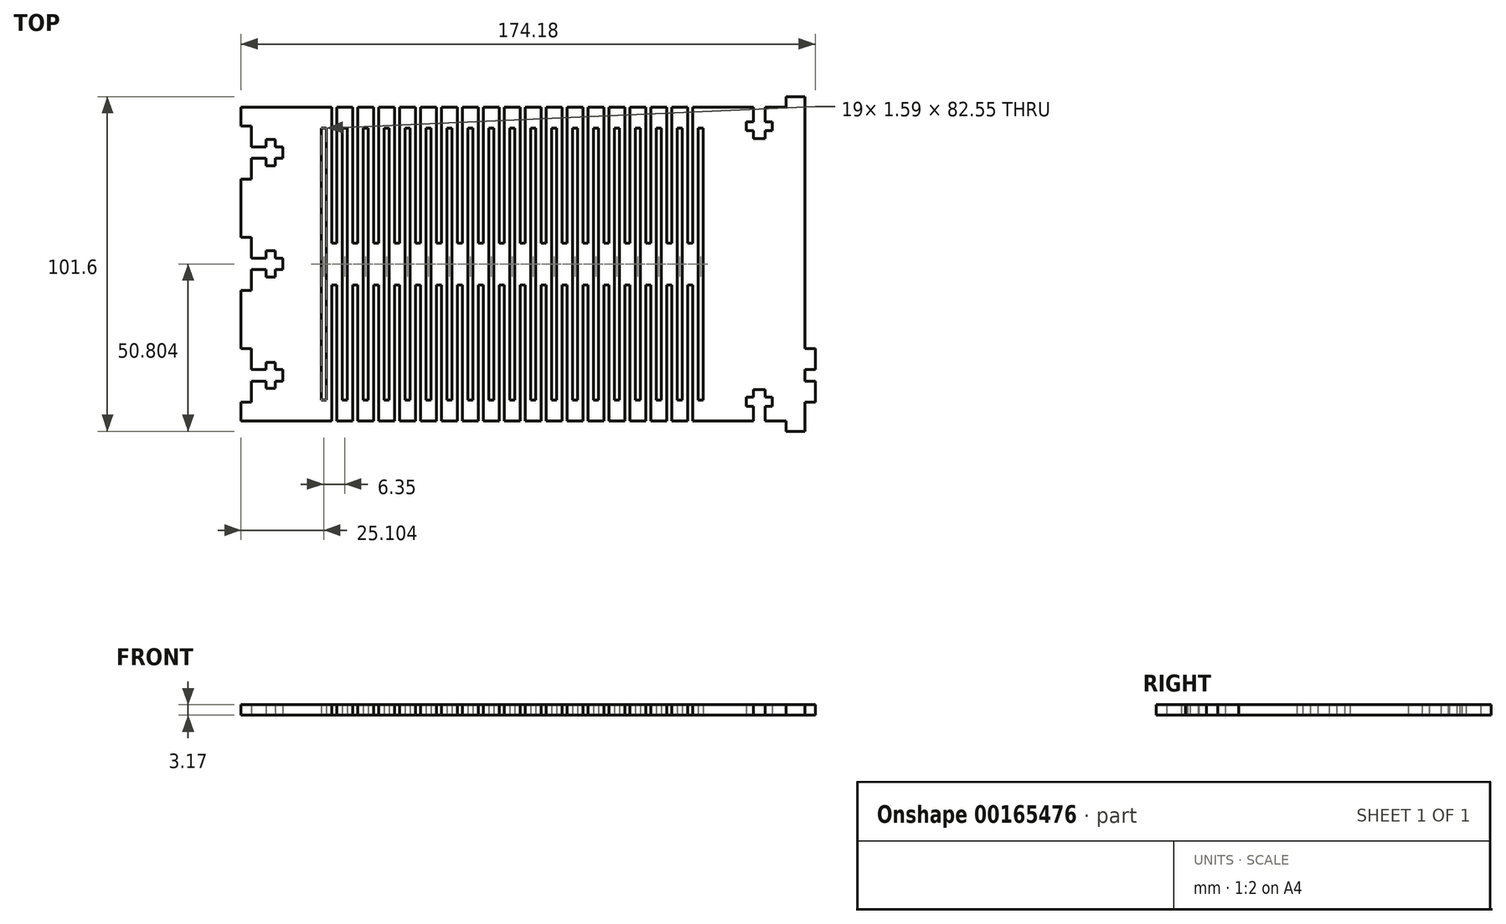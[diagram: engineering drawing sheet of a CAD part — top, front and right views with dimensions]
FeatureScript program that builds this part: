
annotation { "Feature Type Name" : "Feature", "Feature Type Description" : "" }
export const myFeature = defineFeature(function(context is Context, id is Id, definition is map)
    precondition{}
    {
        {
            var Q0;
            Q0=qCreatedBy(makeId("Top.planeOp"),FACE);
            var sketch = newSketch(context, id + "F0", { "sketchPlane" : qUnion([Q0])});
            skLineSegment(sketch, "E0.top", {"start": v(-188.02, -217.63) * mm, "end": v(-188.02, -116.03) * mm});
            skLineSegment(sketch, "E1.bottom", {"start": v(-188.02, -202.39) * mm, "end": v(-188.02, -198.88) * mm});
            skLineSegment(sketch, "E1.top", {"start": v(-175.32, -202.39) * mm, "end": v(-175.32, -198.88) * mm});
            skLineSegment(sketch, "E1.left", {"start": v(-188.02, -202.39) * mm, "end": v(-175.32, -202.39) * mm});
            skLineSegment(sketch, "E1.right", {"start": v(-188.02, -198.88) * mm, "end": v(-175.32, -198.88) * mm});
            skLineSegment(sketch, "E2.bottom", {"start": v(-177.62, -196.66) * mm, "end": v(-177.62, -204.6) * mm});
            skLineSegment(sketch, "E2.top", {"start": v(-180.4, -196.66) * mm, "end": v(-180.4, -204.6) * mm});
            skLineSegment(sketch, "E2.left", {"start": v(-177.62, -196.66) * mm, "end": v(-180.4, -196.66) * mm});
            skLineSegment(sketch, "E2.right", {"start": v(-177.62, -204.6) * mm, "end": v(-180.4, -204.6) * mm});
            skLineSegment(sketch, "E3.bottom", {"start": v(-188.02, -208.74) * mm, "end": v(-188.02, -192.53) * mm});
            skLineSegment(sketch, "E3.top", {"start": v(-184.84, -208.74) * mm, "end": v(-184.84, -192.53) * mm});
            skLineSegment(sketch, "E3.left", {"start": v(-188.02, -208.74) * mm, "end": v(-184.84, -208.74) * mm});
            skLineSegment(sketch, "E3.right", {"start": v(-188.02, -192.53) * mm, "end": v(-184.84, -192.53) * mm});
            skLineSegment(sketch, "E4.bottom", {"start": v(-188.02, -116.03) * mm, "end": v(-13.84, -116.03) * mm});
            skLineSegment(sketch, "E4.top", {"start": v(-188.02, -217.63) * mm, "end": v(-13.84, -217.63) * mm});
            skLineSegment(sketch, "E4.left", {"start": v(-188.02, -116.03) * mm, "end": v(-188.02, -217.63) * mm});
            skLineSegment(sketch, "E4.right", {"start": v(-13.84, -116.03) * mm, "end": v(-13.84, -217.63) * mm});
            skLineSegment(sketch, "E5.0.1.0", {"start": v(-188.02, -174.93) * mm, "end": v(-188.02, -158.72) * mm});
            skLineSegment(sketch, "E5.0.1.1", {"start": v(-184.84, -174.93) * mm, "end": v(-184.84, -158.72) * mm});
            skLineSegment(sketch, "E5.0.1.2", {"start": v(-188.02, -174.93) * mm, "end": v(-184.84, -174.93) * mm});
            skLineSegment(sketch, "E5.0.1.3", {"start": v(-175.32, -168.58) * mm, "end": v(-175.32, -165.07) * mm});
            skLineSegment(sketch, "E5.0.1.4", {"start": v(-188.02, -168.58) * mm, "end": v(-175.32, -168.58) * mm});
            skLineSegment(sketch, "E5.0.1.5", {"start": v(-188.02, -165.07) * mm, "end": v(-175.32, -165.07) * mm});
            skLineSegment(sketch, "E5.0.1.6", {"start": v(-177.62, -162.86) * mm, "end": v(-177.62, -170.8) * mm});
            skLineSegment(sketch, "E5.0.1.7", {"start": v(-180.4, -162.86) * mm, "end": v(-180.4, -170.8) * mm});
            skLineSegment(sketch, "E5.0.1.8", {"start": v(-177.62, -162.86) * mm, "end": v(-180.4, -162.86) * mm});
            skLineSegment(sketch, "E5.0.1.9", {"start": v(-177.62, -170.8) * mm, "end": v(-180.4, -170.8) * mm});
            skLineSegment(sketch, "E5.0.1.10", {"start": v(-188.02, -158.72) * mm, "end": v(-184.84, -158.72) * mm});
            skLineSegment(sketch, "E5.0.1.11", {"start": v(-188.02, -168.58) * mm, "end": v(-188.02, -165.07) * mm});
            skLineSegment(sketch, "E5.0.2.0", {"start": v(-188.02, -141.12) * mm, "end": v(-188.02, -124.92) * mm});
            skLineSegment(sketch, "E5.0.2.1", {"start": v(-184.84, -141.12) * mm, "end": v(-184.84, -124.92) * mm});
            skLineSegment(sketch, "E5.0.2.2", {"start": v(-188.02, -141.12) * mm, "end": v(-184.84, -141.12) * mm});
            skLineSegment(sketch, "E5.0.2.3", {"start": v(-175.32, -134.77) * mm, "end": v(-175.32, -131.27) * mm});
            skLineSegment(sketch, "E5.0.2.4", {"start": v(-188.02, -134.77) * mm, "end": v(-175.32, -134.77) * mm});
            skLineSegment(sketch, "E5.0.2.5", {"start": v(-188.02, -131.27) * mm, "end": v(-175.32, -131.27) * mm});
            skLineSegment(sketch, "E5.0.2.6", {"start": v(-177.62, -129.05) * mm, "end": v(-177.62, -136.99) * mm});
            skLineSegment(sketch, "E5.0.2.7", {"start": v(-180.4, -129.05) * mm, "end": v(-180.4, -136.99) * mm});
            skLineSegment(sketch, "E5.0.2.8", {"start": v(-177.62, -129.05) * mm, "end": v(-180.4, -129.05) * mm});
            skLineSegment(sketch, "E5.0.2.9", {"start": v(-177.62, -136.99) * mm, "end": v(-180.4, -136.99) * mm});
            skLineSegment(sketch, "E5.0.2.10", {"start": v(-188.02, -124.92) * mm, "end": v(-184.84, -124.92) * mm});
            skLineSegment(sketch, "E5.0.2.11", {"start": v(-188.02, -134.77) * mm, "end": v(-188.02, -131.27) * mm});
            skLineSegment(sketch, "E5.direction1", {"start": v(-188.02, -208.74) * mm, "end": v(-162.62, -208.74) * mm, "construction": true});
            skLineSegment(sketch, "E5.direction2", {"start": v(-188.02, -208.74) * mm, "end": v(-188.02, -174.93) * mm, "construction": true});
            skLineSegment(sketch, "E6.bottom", {"start": v(-13.84, -116.03) * mm, "end": v(-17.01, -116.03) * mm});
            skLineSegment(sketch, "E6.top", {"start": v(-13.84, -217.63) * mm, "end": v(-17.01, -217.63) * mm});
            skLineSegment(sketch, "E6.right", {"start": v(-17.01, -116.03) * mm, "end": v(-17.01, -217.63) * mm});
            skLineSegment(sketch, "E7.bottom", {"start": v(-17.01, -208.74) * mm, "end": v(-13.84, -208.74) * mm});
            skLineSegment(sketch, "E7.top", {"start": v(-17.01, -202.39) * mm, "end": v(-13.84, -202.39) * mm});
            skLineSegment(sketch, "E7.left", {"start": v(-17.01, -208.74) * mm, "end": v(-17.01, -202.39) * mm});
            skLineSegment(sketch, "E7.right", {"start": v(-13.84, -208.74) * mm, "end": v(-13.84, -202.39) * mm});
            skLineSegment(sketch, "E8.top", {"start": v(-17.01, -198.88) * mm, "end": v(-13.84, -198.88) * mm});
            skLineSegment(sketch, "E8.left", {"start": v(-17.01, -202.39) * mm, "end": v(-17.01, -198.88) * mm});
            skLineSegment(sketch, "E8.right", {"start": v(-13.84, -202.39) * mm, "end": v(-13.84, -198.88) * mm});
            skLineSegment(sketch, "E9.top", {"start": v(-17.01, -192.53) * mm, "end": v(-13.84, -192.53) * mm});
            skLineSegment(sketch, "E9.left", {"start": v(-17.01, -198.88) * mm, "end": v(-17.01, -192.53) * mm});
            skLineSegment(sketch, "E9.right", {"start": v(-13.84, -198.88) * mm, "end": v(-13.84, -192.53) * mm});
            skLineSegment(sketch, "E10.0.1.0", {"start": v(-13.84, -168.58) * mm, "end": v(-13.84, -165.07) * mm});
            skLineSegment(sketch, "E10.0.1.1", {"start": v(-17.01, -168.58) * mm, "end": v(-17.01, -165.07) * mm});
            skLineSegment(sketch, "E10.0.1.2", {"start": v(-17.01, -174.93) * mm, "end": v(-17.01, -168.58) * mm});
            skLineSegment(sketch, "E10.0.1.3", {"start": v(-17.01, -168.58) * mm, "end": v(-13.84, -168.58) * mm});
            skLineSegment(sketch, "E10.0.1.4", {"start": v(-17.01, -174.93) * mm, "end": v(-13.84, -174.93) * mm});
            skLineSegment(sketch, "E10.0.1.5", {"start": v(-13.84, -174.93) * mm, "end": v(-13.84, -168.58) * mm});
            skLineSegment(sketch, "E10.0.1.6", {"start": v(-13.84, -165.07) * mm, "end": v(-13.84, -158.72) * mm});
            skLineSegment(sketch, "E10.0.1.7", {"start": v(-17.01, -158.72) * mm, "end": v(-13.84, -158.72) * mm});
            skLineSegment(sketch, "E10.0.1.8", {"start": v(-17.01, -165.07) * mm, "end": v(-17.01, -158.72) * mm});
            skLineSegment(sketch, "E10.0.1.9", {"start": v(-17.01, -165.07) * mm, "end": v(-13.84, -165.07) * mm});
            skLineSegment(sketch, "E10.0.1.10", {"start": v(-17.01, -165.07) * mm, "end": v(-13.84, -165.07) * mm});
            skLineSegment(sketch, "E10.0.1.11", {"start": v(-17.01, -168.58) * mm, "end": v(-13.84, -168.58) * mm});
            skLineSegment(sketch, "E10.0.2.0", {"start": v(-13.84, -134.77) * mm, "end": v(-13.84, -131.27) * mm});
            skLineSegment(sketch, "E10.0.2.1", {"start": v(-17.01, -134.77) * mm, "end": v(-17.01, -131.27) * mm});
            skLineSegment(sketch, "E10.0.2.2", {"start": v(-17.01, -141.12) * mm, "end": v(-17.01, -134.77) * mm});
            skLineSegment(sketch, "E10.0.2.3", {"start": v(-17.01, -134.77) * mm, "end": v(-13.84, -134.77) * mm});
            skLineSegment(sketch, "E10.0.2.4", {"start": v(-17.01, -141.12) * mm, "end": v(-13.84, -141.12) * mm});
            skLineSegment(sketch, "E10.0.2.5", {"start": v(-13.84, -141.12) * mm, "end": v(-13.84, -134.77) * mm});
            skLineSegment(sketch, "E10.0.2.6", {"start": v(-13.84, -131.27) * mm, "end": v(-13.84, -124.92) * mm});
            skLineSegment(sketch, "E10.0.2.7", {"start": v(-17.01, -124.92) * mm, "end": v(-13.84, -124.92) * mm});
            skLineSegment(sketch, "E10.0.2.8", {"start": v(-17.01, -131.27) * mm, "end": v(-17.01, -124.92) * mm});
            skLineSegment(sketch, "E10.0.2.9", {"start": v(-17.01, -131.27) * mm, "end": v(-13.84, -131.27) * mm});
            skLineSegment(sketch, "E10.0.2.10", {"start": v(-17.01, -131.27) * mm, "end": v(-13.84, -131.27) * mm});
            skLineSegment(sketch, "E10.0.2.11", {"start": v(-17.01, -134.77) * mm, "end": v(-13.84, -134.77) * mm});
            skLineSegment(sketch, "E10.direction1", {"start": v(-17.01, -208.74) * mm, "end": v(373.75, -208.74) * mm, "construction": true});
            skLineSegment(sketch, "E10.direction2", {"start": v(-17.01, -208.74) * mm, "end": v(-17.01, -174.93) * mm, "construction": true});
            skLineSegment(sketch, "E11.top", {"start": v(-188.02, -119.2) * mm, "end": v(-13.84, -119.2) * mm});
            skLineSegment(sketch, "E11.left", {"start": v(-188.02, -116.03) * mm, "end": v(-188.02, -119.2) * mm});
            skLineSegment(sketch, "E11.right", {"start": v(-13.84, -116.03) * mm, "end": v(-13.84, -119.2) * mm});
            skLineSegment(sketch, "E12.top", {"start": v(-188.02, -214.45) * mm, "end": v(-13.84, -214.45) * mm});
            skLineSegment(sketch, "E12.left", {"start": v(-188.02, -217.63) * mm, "end": v(-188.02, -214.45) * mm});
            skLineSegment(sketch, "E12.right", {"start": v(-13.84, -217.63) * mm, "end": v(-13.84, -214.45) * mm});
            skLineSegment(sketch, "E13.bottom", {"start": v(-29.08, -217.63) * mm, "end": v(-32.58, -217.63) * mm});
            skLineSegment(sketch, "E13.top", {"start": v(-29.08, -204.93) * mm, "end": v(-32.58, -204.93) * mm});
            skLineSegment(sketch, "E13.left", {"start": v(-29.08, -217.63) * mm, "end": v(-29.08, -204.93) * mm});
            skLineSegment(sketch, "E13.right", {"start": v(-32.58, -217.63) * mm, "end": v(-32.58, -204.93) * mm});
            skLineSegment(sketch, "E14.bottom", {"start": v(-34.8, -207.23) * mm, "end": v(-26.86, -207.23) * mm});
            skLineSegment(sketch, "E14.top", {"start": v(-34.8, -210) * mm, "end": v(-26.86, -210) * mm});
            skLineSegment(sketch, "E14.left", {"start": v(-34.8, -207.23) * mm, "end": v(-34.8, -210) * mm});
            skLineSegment(sketch, "E14.right", {"start": v(-26.86, -207.23) * mm, "end": v(-26.86, -210) * mm});
            skLineSegment(sketch, "E15.bottom", {"start": v(-22.73, -217.63) * mm, "end": v(-38.93, -217.63) * mm});
            skLineSegment(sketch, "E15.top", {"start": v(-22.73, -214.45) * mm, "end": v(-38.93, -214.45) * mm});
            skLineSegment(sketch, "E15.left", {"start": v(-22.73, -217.63) * mm, "end": v(-22.73, -214.45) * mm});
            skLineSegment(sketch, "E15.right", {"start": v(-38.93, -217.63) * mm, "end": v(-38.93, -214.45) * mm});
            skLineSegment(sketch, "E16", {"start": v(366.52, -166.83) * mm, "end": v(393.67, -166.83) * mm});
            skLineSegment(sketch, "E17.MirrorCS", {"start": v(-29.08, -116.03) * mm, "end": v(-32.58, -116.03) * mm});
            skLineSegment(sketch, "E18.MirrorCS", {"start": v(-29.08, -128.73) * mm, "end": v(-32.58, -128.73) * mm});
            skLineSegment(sketch, "E19.MirrorCS", {"start": v(-29.08, -116.03) * mm, "end": v(-29.08, -128.73) * mm});
            skLineSegment(sketch, "E20.MirrorCS", {"start": v(-32.58, -116.03) * mm, "end": v(-32.58, -128.73) * mm});
            skLineSegment(sketch, "E21.MirrorCS", {"start": v(-34.8, -126.42) * mm, "end": v(-26.86, -126.42) * mm});
            skLineSegment(sketch, "E22.MirrorCS", {"start": v(-34.8, -123.65) * mm, "end": v(-26.86, -123.65) * mm});
            skLineSegment(sketch, "E23.MirrorCS", {"start": v(-22.73, -116.03) * mm, "end": v(-38.93, -116.03) * mm});
            skLineSegment(sketch, "E24.MirrorCS", {"start": v(-26.86, -126.42) * mm, "end": v(-26.86, -123.65) * mm});
            skLineSegment(sketch, "E25.MirrorCS", {"start": v(-34.8, -126.42) * mm, "end": v(-34.8, -123.65) * mm});
            skLineSegment(sketch, "E26.MirrorCS", {"start": v(-22.73, -119.2) * mm, "end": v(-38.93, -119.2) * mm});
            skLineSegment(sketch, "E27.MirrorCS", {"start": v(-22.73, -116.03) * mm, "end": v(-22.73, -119.2) * mm});
            skLineSegment(sketch, "E28.MirrorCS", {"start": v(-38.93, -116.03) * mm, "end": v(-38.93, -119.2) * mm});
            skLineSegment(sketch, "E29.bottom", {"start": v(-38.93, -119.2) * mm, "end": v(-47.82, -119.2) * mm});
            skLineSegment(sketch, "E29.top", {"start": v(-38.93, -116.03) * mm, "end": v(-47.82, -116.03) * mm});
            skLineSegment(sketch, "E29.left", {"start": v(-38.93, -119.2) * mm, "end": v(-38.93, -116.03) * mm});
            skLineSegment(sketch, "E29.right", {"start": v(-47.82, -119.2) * mm, "end": v(-47.82, -116.03) * mm});
            skLineSegment(sketch, "E30.bottom", {"start": v(-38.93, -217.63) * mm, "end": v(-47.82, -217.63) * mm});
            skLineSegment(sketch, "E30.top", {"start": v(-38.93, -214.45) * mm, "end": v(-47.82, -214.45) * mm});
            skLineSegment(sketch, "E30.right", {"start": v(-47.82, -217.63) * mm, "end": v(-47.82, -214.45) * mm});
            skLineSegment(sketch, "E31.bottom", {"start": v(-179.13, -217.63) * mm, "end": v(-172.78, -217.63) * mm});
            skLineSegment(sketch, "E31.top", {"start": v(-179.13, -214.45) * mm, "end": v(-172.78, -214.45) * mm});
            skLineSegment(sketch, "E31.left", {"start": v(-179.13, -217.63) * mm, "end": v(-179.13, -214.45) * mm});
            skLineSegment(sketch, "E31.right", {"start": v(-172.78, -217.63) * mm, "end": v(-172.78, -214.45) * mm});
            skLineSegment(sketch, "E32.bottom", {"start": v(-172.78, -217.63) * mm, "end": v(-169.27, -217.63) * mm});
            skLineSegment(sketch, "E32.top", {"start": v(-172.78, -214.45) * mm, "end": v(-169.27, -214.45) * mm});
            skLineSegment(sketch, "E32.right", {"start": v(-169.27, -217.63) * mm, "end": v(-169.27, -214.45) * mm});
            skLineSegment(sketch, "E33.bottom", {"start": v(-169.27, -217.63) * mm, "end": v(-162.92, -217.63) * mm});
            skLineSegment(sketch, "E33.top", {"start": v(-169.27, -214.45) * mm, "end": v(-162.92, -214.45) * mm});
            skLineSegment(sketch, "E33.right", {"start": v(-162.92, -217.63) * mm, "end": v(-162.92, -214.45) * mm});
            skLineSegment(sketch, "E34.MirrorCS", {"start": v(-172.78, -116.03) * mm, "end": v(-172.78, -119.2) * mm});
            skLineSegment(sketch, "E35.MirrorCS", {"start": v(-169.27, -116.03) * mm, "end": v(-169.27, -119.2) * mm});
            skLineSegment(sketch, "E36.MirrorCS", {"start": v(-179.13, -116.03) * mm, "end": v(-172.78, -116.03) * mm});
            skLineSegment(sketch, "E37.MirrorCS", {"start": v(-179.13, -119.2) * mm, "end": v(-172.78, -119.2) * mm});
            skLineSegment(sketch, "E38.MirrorCS", {"start": v(-179.13, -116.03) * mm, "end": v(-179.13, -119.2) * mm});
            skLineSegment(sketch, "E39.MirrorCS", {"start": v(-169.27, -116.03) * mm, "end": v(-162.92, -116.03) * mm});
            skLineSegment(sketch, "E40.MirrorCS", {"start": v(-172.78, -116.03) * mm, "end": v(-169.27, -116.03) * mm});
            skLineSegment(sketch, "E41.MirrorCS", {"start": v(-169.27, -119.2) * mm, "end": v(-162.92, -119.2) * mm});
            skLineSegment(sketch, "E42.MirrorCS", {"start": v(-162.92, -116.03) * mm, "end": v(-162.92, -119.2) * mm});
            skLineSegment(sketch, "E43.MirrorCS", {"start": v(-172.78, -119.2) * mm, "end": v(-169.27, -119.2) * mm});
            skLineSegment(sketch, "E44.bottom", {"start": v(-52.58, -116.03) * mm, "end": v(-51, -116.03) * mm});
            skLineSegment(sketch, "E44.top", {"start": v(-52.58, -160.48) * mm, "end": v(-51, -160.48) * mm});
            skLineSegment(sketch, "E44.left", {"start": v(-52.58, -116.03) * mm, "end": v(-52.58, -160.48) * mm});
            skLineSegment(sketch, "E44.right", {"start": v(-51, -116.03) * mm, "end": v(-51, -160.48) * mm});
            skLineSegment(sketch, "E45.bottom", {"start": v(-52.58, -217.63) * mm, "end": v(-51, -217.63) * mm});
            skLineSegment(sketch, "E45.top", {"start": v(-52.58, -173.18) * mm, "end": v(-51, -173.18) * mm});
            skLineSegment(sketch, "E45.left", {"start": v(-52.58, -217.63) * mm, "end": v(-52.58, -173.18) * mm});
            skLineSegment(sketch, "E45.right", {"start": v(-51, -217.63) * mm, "end": v(-51, -173.18) * mm});
            skLineSegment(sketch, "E46.bottom", {"start": v(-49.4, -125.55) * mm, "end": v(-47.82, -125.55) * mm});
            skLineSegment(sketch, "E46.top", {"start": v(-49.4, -208.1) * mm, "end": v(-47.82, -208.1) * mm});
            skLineSegment(sketch, "E46.left", {"start": v(-49.4, -125.55) * mm, "end": v(-49.4, -208.1) * mm});
            skLineSegment(sketch, "E46.right", {"start": v(-47.82, -125.55) * mm, "end": v(-47.82, -208.1) * mm});
            skLineSegment(sketch, "E47.1.0.0", {"start": v(-57.35, -217.63) * mm, "end": v(-57.35, -173.18) * mm});
            skLineSegment(sketch, "E47.1.0.1", {"start": v(-57.35, -116.03) * mm, "end": v(-57.35, -160.48) * mm});
            skLineSegment(sketch, "E47.1.0.2", {"start": v(-54.17, -125.55) * mm, "end": v(-54.17, -208.1) * mm});
            skLineSegment(sketch, "E47.1.0.3", {"start": v(-58.93, -116.03) * mm, "end": v(-58.93, -160.48) * mm});
            skLineSegment(sketch, "E47.1.0.4", {"start": v(-55.76, -125.55) * mm, "end": v(-55.76, -208.1) * mm});
            skLineSegment(sketch, "E47.1.0.5", {"start": v(-58.93, -217.63) * mm, "end": v(-58.93, -173.18) * mm});
            skLineSegment(sketch, "E47.1.0.6", {"start": v(-58.93, -116.03) * mm, "end": v(-57.35, -116.03) * mm});
            skLineSegment(sketch, "E47.1.0.7", {"start": v(-58.93, -217.63) * mm, "end": v(-57.35, -217.63) * mm});
            skLineSegment(sketch, "E47.1.0.8", {"start": v(-58.93, -173.18) * mm, "end": v(-57.35, -173.18) * mm});
            skLineSegment(sketch, "E47.1.0.9", {"start": v(-58.93, -160.48) * mm, "end": v(-57.35, -160.48) * mm});
            skLineSegment(sketch, "E47.1.0.10", {"start": v(-55.76, -208.1) * mm, "end": v(-54.17, -208.1) * mm});
            skLineSegment(sketch, "E47.1.0.11", {"start": v(-55.76, -125.55) * mm, "end": v(-54.17, -125.55) * mm});
            skLineSegment(sketch, "E47.2.0.0", {"start": v(-63.7, -217.63) * mm, "end": v(-63.7, -173.18) * mm});
            skLineSegment(sketch, "E47.2.0.1", {"start": v(-63.7, -116.03) * mm, "end": v(-63.7, -160.48) * mm});
            skLineSegment(sketch, "E47.2.0.2", {"start": v(-60.52, -125.55) * mm, "end": v(-60.52, -208.1) * mm});
            skLineSegment(sketch, "E47.2.0.3", {"start": v(-65.28, -116.03) * mm, "end": v(-65.28, -160.48) * mm});
            skLineSegment(sketch, "E47.2.0.4", {"start": v(-62.1, -125.55) * mm, "end": v(-62.1, -208.1) * mm});
            skLineSegment(sketch, "E47.2.0.5", {"start": v(-65.28, -217.63) * mm, "end": v(-65.28, -173.18) * mm});
            skLineSegment(sketch, "E47.2.0.6", {"start": v(-65.28, -116.03) * mm, "end": v(-63.7, -116.03) * mm});
            skLineSegment(sketch, "E47.2.0.7", {"start": v(-65.28, -217.63) * mm, "end": v(-63.7, -217.63) * mm});
            skLineSegment(sketch, "E47.2.0.8", {"start": v(-65.28, -173.18) * mm, "end": v(-63.7, -173.18) * mm});
            skLineSegment(sketch, "E47.2.0.9", {"start": v(-65.28, -160.48) * mm, "end": v(-63.7, -160.48) * mm});
            skLineSegment(sketch, "E47.2.0.10", {"start": v(-62.1, -208.1) * mm, "end": v(-60.52, -208.1) * mm});
            skLineSegment(sketch, "E47.2.0.11", {"start": v(-62.1, -125.55) * mm, "end": v(-60.52, -125.55) * mm});
            skLineSegment(sketch, "E47.3.0.0", {"start": v(-70.05, -217.63) * mm, "end": v(-70.05, -173.18) * mm});
            skLineSegment(sketch, "E47.3.0.1", {"start": v(-70.05, -116.03) * mm, "end": v(-70.05, -160.48) * mm});
            skLineSegment(sketch, "E47.3.0.2", {"start": v(-66.87, -125.55) * mm, "end": v(-66.87, -208.1) * mm});
            skLineSegment(sketch, "E47.3.0.3", {"start": v(-71.63, -116.03) * mm, "end": v(-71.63, -160.48) * mm});
            skLineSegment(sketch, "E47.3.0.4", {"start": v(-68.46, -125.55) * mm, "end": v(-68.46, -208.1) * mm});
            skLineSegment(sketch, "E47.3.0.5", {"start": v(-71.63, -217.63) * mm, "end": v(-71.63, -173.18) * mm});
            skLineSegment(sketch, "E47.3.0.6", {"start": v(-71.63, -116.03) * mm, "end": v(-70.05, -116.03) * mm});
            skLineSegment(sketch, "E47.3.0.7", {"start": v(-71.63, -217.63) * mm, "end": v(-70.05, -217.63) * mm});
            skLineSegment(sketch, "E47.3.0.8", {"start": v(-71.63, -173.18) * mm, "end": v(-70.05, -173.18) * mm});
            skLineSegment(sketch, "E47.3.0.9", {"start": v(-71.63, -160.48) * mm, "end": v(-70.05, -160.48) * mm});
            skLineSegment(sketch, "E47.3.0.10", {"start": v(-68.46, -208.1) * mm, "end": v(-66.87, -208.1) * mm});
            skLineSegment(sketch, "E47.3.0.11", {"start": v(-68.46, -125.55) * mm, "end": v(-66.87, -125.55) * mm});
            skLineSegment(sketch, "E47.4.0.0", {"start": v(-76.4, -217.63) * mm, "end": v(-76.4, -173.18) * mm});
            skLineSegment(sketch, "E47.4.0.1", {"start": v(-76.4, -116.03) * mm, "end": v(-76.4, -160.48) * mm});
            skLineSegment(sketch, "E47.4.0.2", {"start": v(-73.22, -125.55) * mm, "end": v(-73.22, -208.1) * mm});
            skLineSegment(sketch, "E47.4.0.3", {"start": v(-77.98, -116.03) * mm, "end": v(-77.98, -160.48) * mm});
            skLineSegment(sketch, "E47.4.0.4", {"start": v(-74.8, -125.55) * mm, "end": v(-74.8, -208.1) * mm});
            skLineSegment(sketch, "E47.4.0.5", {"start": v(-77.98, -217.63) * mm, "end": v(-77.98, -173.18) * mm});
            skLineSegment(sketch, "E47.4.0.6", {"start": v(-77.98, -116.03) * mm, "end": v(-76.4, -116.03) * mm});
            skLineSegment(sketch, "E47.4.0.7", {"start": v(-77.98, -217.63) * mm, "end": v(-76.4, -217.63) * mm});
            skLineSegment(sketch, "E47.4.0.8", {"start": v(-77.98, -173.18) * mm, "end": v(-76.4, -173.18) * mm});
            skLineSegment(sketch, "E47.4.0.9", {"start": v(-77.98, -160.48) * mm, "end": v(-76.4, -160.48) * mm});
            skLineSegment(sketch, "E47.4.0.10", {"start": v(-74.8, -208.1) * mm, "end": v(-73.22, -208.1) * mm});
            skLineSegment(sketch, "E47.4.0.11", {"start": v(-74.8, -125.55) * mm, "end": v(-73.22, -125.55) * mm});
            skLineSegment(sketch, "E47.5.0.0", {"start": v(-82.75, -217.63) * mm, "end": v(-82.75, -173.18) * mm});
            skLineSegment(sketch, "E47.5.0.1", {"start": v(-82.75, -116.03) * mm, "end": v(-82.75, -160.48) * mm});
            skLineSegment(sketch, "E47.5.0.2", {"start": v(-79.57, -125.55) * mm, "end": v(-79.57, -208.1) * mm});
            skLineSegment(sketch, "E47.5.0.3", {"start": v(-84.33, -116.03) * mm, "end": v(-84.33, -160.48) * mm});
            skLineSegment(sketch, "E47.5.0.4", {"start": v(-81.16, -125.55) * mm, "end": v(-81.16, -208.1) * mm});
            skLineSegment(sketch, "E47.5.0.5", {"start": v(-84.33, -217.63) * mm, "end": v(-84.33, -173.18) * mm});
            skLineSegment(sketch, "E47.5.0.6", {"start": v(-84.33, -116.03) * mm, "end": v(-82.75, -116.03) * mm});
            skLineSegment(sketch, "E47.5.0.7", {"start": v(-84.33, -217.63) * mm, "end": v(-82.75, -217.63) * mm});
            skLineSegment(sketch, "E47.5.0.8", {"start": v(-84.33, -173.18) * mm, "end": v(-82.75, -173.18) * mm});
            skLineSegment(sketch, "E47.5.0.9", {"start": v(-84.33, -160.48) * mm, "end": v(-82.75, -160.48) * mm});
            skLineSegment(sketch, "E47.5.0.10", {"start": v(-81.16, -208.1) * mm, "end": v(-79.57, -208.1) * mm});
            skLineSegment(sketch, "E47.5.0.11", {"start": v(-81.16, -125.55) * mm, "end": v(-79.57, -125.55) * mm});
            skLineSegment(sketch, "E47.6.0.0", {"start": v(-89.1, -217.63) * mm, "end": v(-89.1, -173.18) * mm});
            skLineSegment(sketch, "E47.6.0.1", {"start": v(-89.1, -116.03) * mm, "end": v(-89.1, -160.48) * mm});
            skLineSegment(sketch, "E47.6.0.2", {"start": v(-85.92, -125.55) * mm, "end": v(-85.92, -208.1) * mm});
            skLineSegment(sketch, "E47.6.0.3", {"start": v(-90.68, -116.03) * mm, "end": v(-90.68, -160.48) * mm});
            skLineSegment(sketch, "E47.6.0.4", {"start": v(-87.5, -125.55) * mm, "end": v(-87.5, -208.1) * mm});
            skLineSegment(sketch, "E47.6.0.5", {"start": v(-90.68, -217.63) * mm, "end": v(-90.68, -173.18) * mm});
            skLineSegment(sketch, "E47.6.0.6", {"start": v(-90.68, -116.03) * mm, "end": v(-89.1, -116.03) * mm});
            skLineSegment(sketch, "E47.6.0.7", {"start": v(-90.68, -217.63) * mm, "end": v(-89.1, -217.63) * mm});
            skLineSegment(sketch, "E47.6.0.8", {"start": v(-90.68, -173.18) * mm, "end": v(-89.1, -173.18) * mm});
            skLineSegment(sketch, "E47.6.0.9", {"start": v(-90.68, -160.48) * mm, "end": v(-89.1, -160.48) * mm});
            skLineSegment(sketch, "E47.6.0.10", {"start": v(-87.5, -208.1) * mm, "end": v(-85.92, -208.1) * mm});
            skLineSegment(sketch, "E47.6.0.11", {"start": v(-87.5, -125.55) * mm, "end": v(-85.92, -125.55) * mm});
            skLineSegment(sketch, "E47.7.0.0", {"start": v(-95.45, -217.63) * mm, "end": v(-95.45, -173.18) * mm});
            skLineSegment(sketch, "E47.7.0.1", {"start": v(-95.45, -116.03) * mm, "end": v(-95.45, -160.48) * mm});
            skLineSegment(sketch, "E47.7.0.2", {"start": v(-92.27, -125.55) * mm, "end": v(-92.27, -208.1) * mm});
            skLineSegment(sketch, "E47.7.0.3", {"start": v(-97.03, -116.03) * mm, "end": v(-97.03, -160.48) * mm});
            skLineSegment(sketch, "E47.7.0.4", {"start": v(-93.86, -125.55) * mm, "end": v(-93.86, -208.1) * mm});
            skLineSegment(sketch, "E47.7.0.5", {"start": v(-97.03, -217.63) * mm, "end": v(-97.03, -173.18) * mm});
            skLineSegment(sketch, "E47.7.0.6", {"start": v(-97.03, -116.03) * mm, "end": v(-95.45, -116.03) * mm});
            skLineSegment(sketch, "E47.7.0.7", {"start": v(-97.03, -217.63) * mm, "end": v(-95.45, -217.63) * mm});
            skLineSegment(sketch, "E47.7.0.8", {"start": v(-97.03, -173.18) * mm, "end": v(-95.45, -173.18) * mm});
            skLineSegment(sketch, "E47.7.0.9", {"start": v(-97.03, -160.48) * mm, "end": v(-95.45, -160.48) * mm});
            skLineSegment(sketch, "E47.7.0.10", {"start": v(-93.86, -208.1) * mm, "end": v(-92.27, -208.1) * mm});
            skLineSegment(sketch, "E47.7.0.11", {"start": v(-93.86, -125.55) * mm, "end": v(-92.27, -125.55) * mm});
            skLineSegment(sketch, "E47.direction1", {"start": v(-52.58, -217.63) * mm, "end": v(-58.93, -217.63) * mm, "construction": true});
            skLineSegment(sketch, "E48.bottom", {"start": v(-162.92, -119.2) * mm, "end": v(-155.3, -119.2) * mm});
            skLineSegment(sketch, "E48.top", {"start": v(-162.92, -116.03) * mm, "end": v(-155.3, -116.03) * mm});
            skLineSegment(sketch, "E48.left", {"start": v(-162.92, -119.2) * mm, "end": v(-162.92, -116.03) * mm});
            skLineSegment(sketch, "E49.6.8.0", {"start": v(-98.62, -125.55) * mm, "end": v(-98.62, -208.1) * mm});
            skLineSegment(sketch, "E49.12.8.0", {"start": v(-100.2, -125.55) * mm, "end": v(-100.2, -208.1) * mm});
            skLineSegment(sketch, "E49.30.8.0", {"start": v(-100.2, -208.1) * mm, "end": v(-98.62, -208.1) * mm});
            skLineSegment(sketch, "E49.33.8.0", {"start": v(-100.2, -125.55) * mm, "end": v(-98.62, -125.55) * mm});
            skLineSegment(sketch, "E50.0.9.0", {"start": v(-108.15, -217.63) * mm, "end": v(-108.15, -173.18) * mm});
            skLineSegment(sketch, "E50.3.9.0", {"start": v(-108.15, -116.03) * mm, "end": v(-108.15, -160.48) * mm});
            skLineSegment(sketch, "E50.6.9.0", {"start": v(-104.97, -125.55) * mm, "end": v(-104.97, -208.1) * mm});
            skLineSegment(sketch, "E50.9.9.0", {"start": v(-109.73, -116.03) * mm, "end": v(-109.73, -160.48) * mm});
            skLineSegment(sketch, "E50.12.9.0", {"start": v(-106.56, -125.55) * mm, "end": v(-106.56, -208.1) * mm});
            skLineSegment(sketch, "E50.15.9.0", {"start": v(-109.73, -217.63) * mm, "end": v(-109.73, -173.18) * mm});
            skLineSegment(sketch, "E50.18.9.0", {"start": v(-109.73, -116.03) * mm, "end": v(-108.15, -116.03) * mm});
            skLineSegment(sketch, "E50.21.9.0", {"start": v(-109.73, -217.63) * mm, "end": v(-108.15, -217.63) * mm});
            skLineSegment(sketch, "E50.24.9.0", {"start": v(-109.73, -173.18) * mm, "end": v(-108.15, -173.18) * mm});
            skLineSegment(sketch, "E50.27.9.0", {"start": v(-109.73, -160.48) * mm, "end": v(-108.15, -160.48) * mm});
            skLineSegment(sketch, "E50.30.9.0", {"start": v(-106.56, -208.1) * mm, "end": v(-104.97, -208.1) * mm});
            skLineSegment(sketch, "E50.33.9.0", {"start": v(-106.56, -125.55) * mm, "end": v(-104.97, -125.55) * mm});
            skLineSegment(sketch, "E51.0.10.0", {"start": v(-114.5, -217.63) * mm, "end": v(-114.5, -173.18) * mm});
            skLineSegment(sketch, "E51.3.10.0", {"start": v(-114.5, -116.03) * mm, "end": v(-114.5, -160.48) * mm});
            skLineSegment(sketch, "E51.6.10.0", {"start": v(-111.32, -125.55) * mm, "end": v(-111.32, -208.1) * mm});
            skLineSegment(sketch, "E51.9.10.0", {"start": v(-116.08, -116.03) * mm, "end": v(-116.08, -160.48) * mm});
            skLineSegment(sketch, "E51.12.10.0", {"start": v(-112.9, -125.55) * mm, "end": v(-112.9, -208.1) * mm});
            skLineSegment(sketch, "E51.15.10.0", {"start": v(-116.08, -217.63) * mm, "end": v(-116.08, -173.18) * mm});
            skLineSegment(sketch, "E51.18.10.0", {"start": v(-116.08, -116.03) * mm, "end": v(-114.5, -116.03) * mm});
            skLineSegment(sketch, "E51.21.10.0", {"start": v(-116.08, -217.63) * mm, "end": v(-114.5, -217.63) * mm});
            skLineSegment(sketch, "E51.24.10.0", {"start": v(-116.08, -173.18) * mm, "end": v(-114.5, -173.18) * mm});
            skLineSegment(sketch, "E51.27.10.0", {"start": v(-116.08, -160.48) * mm, "end": v(-114.5, -160.48) * mm});
            skLineSegment(sketch, "E51.30.10.0", {"start": v(-112.9, -208.1) * mm, "end": v(-111.32, -208.1) * mm});
            skLineSegment(sketch, "E51.33.10.0", {"start": v(-112.9, -125.55) * mm, "end": v(-111.32, -125.55) * mm});
            skLineSegment(sketch, "E51.0.11.0", {"start": v(-120.85, -217.63) * mm, "end": v(-120.85, -173.18) * mm});
            skLineSegment(sketch, "E51.3.11.0", {"start": v(-120.85, -116.03) * mm, "end": v(-120.85, -160.48) * mm});
            skLineSegment(sketch, "E51.6.11.0", {"start": v(-117.67, -125.55) * mm, "end": v(-117.67, -208.1) * mm});
            skLineSegment(sketch, "E51.9.11.0", {"start": v(-122.43, -116.03) * mm, "end": v(-122.43, -160.48) * mm});
            skLineSegment(sketch, "E51.12.11.0", {"start": v(-119.26, -125.55) * mm, "end": v(-119.26, -208.1) * mm});
            skLineSegment(sketch, "E51.15.11.0", {"start": v(-122.43, -217.63) * mm, "end": v(-122.43, -173.18) * mm});
            skLineSegment(sketch, "E51.18.11.0", {"start": v(-122.43, -116.03) * mm, "end": v(-120.85, -116.03) * mm});
            skLineSegment(sketch, "E51.21.11.0", {"start": v(-122.43, -217.63) * mm, "end": v(-120.85, -217.63) * mm});
            skLineSegment(sketch, "E51.24.11.0", {"start": v(-122.43, -173.18) * mm, "end": v(-120.85, -173.18) * mm});
            skLineSegment(sketch, "E51.27.11.0", {"start": v(-122.43, -160.48) * mm, "end": v(-120.85, -160.48) * mm});
            skLineSegment(sketch, "E51.30.11.0", {"start": v(-119.26, -208.1) * mm, "end": v(-117.67, -208.1) * mm});
            skLineSegment(sketch, "E51.33.11.0", {"start": v(-119.26, -125.55) * mm, "end": v(-117.67, -125.55) * mm});
            skLineSegment(sketch, "E51.0.12.0", {"start": v(-127.2, -217.63) * mm, "end": v(-127.2, -173.18) * mm});
            skLineSegment(sketch, "E51.3.12.0", {"start": v(-127.2, -116.03) * mm, "end": v(-127.2, -160.48) * mm});
            skLineSegment(sketch, "E51.6.12.0", {"start": v(-124.02, -125.55) * mm, "end": v(-124.02, -208.1) * mm});
            skLineSegment(sketch, "E51.9.12.0", {"start": v(-128.78, -116.03) * mm, "end": v(-128.78, -160.48) * mm});
            skLineSegment(sketch, "E51.12.12.0", {"start": v(-125.6, -125.55) * mm, "end": v(-125.6, -208.1) * mm});
            skLineSegment(sketch, "E51.15.12.0", {"start": v(-128.78, -217.63) * mm, "end": v(-128.78, -173.18) * mm});
            skLineSegment(sketch, "E51.18.12.0", {"start": v(-128.78, -116.03) * mm, "end": v(-127.2, -116.03) * mm});
            skLineSegment(sketch, "E51.21.12.0", {"start": v(-128.78, -217.63) * mm, "end": v(-127.2, -217.63) * mm});
            skLineSegment(sketch, "E51.24.12.0", {"start": v(-128.78, -173.18) * mm, "end": v(-127.2, -173.18) * mm});
            skLineSegment(sketch, "E51.27.12.0", {"start": v(-128.78, -160.48) * mm, "end": v(-127.2, -160.48) * mm});
            skLineSegment(sketch, "E51.30.12.0", {"start": v(-125.6, -208.1) * mm, "end": v(-124.02, -208.1) * mm});
            skLineSegment(sketch, "E51.33.12.0", {"start": v(-125.6, -125.55) * mm, "end": v(-124.02, -125.55) * mm});
            skLineSegment(sketch, "E51.0.13.0", {"start": v(-133.55, -217.63) * mm, "end": v(-133.55, -173.18) * mm});
            skLineSegment(sketch, "E51.3.13.0", {"start": v(-133.55, -116.03) * mm, "end": v(-133.55, -160.48) * mm});
            skLineSegment(sketch, "E51.6.13.0", {"start": v(-130.37, -125.55) * mm, "end": v(-130.37, -208.1) * mm});
            skLineSegment(sketch, "E51.9.13.0", {"start": v(-135.13, -116.03) * mm, "end": v(-135.13, -160.48) * mm});
            skLineSegment(sketch, "E51.12.13.0", {"start": v(-131.96, -125.55) * mm, "end": v(-131.96, -208.1) * mm});
            skLineSegment(sketch, "E51.15.13.0", {"start": v(-135.13, -217.63) * mm, "end": v(-135.13, -173.18) * mm});
            skLineSegment(sketch, "E51.18.13.0", {"start": v(-135.13, -116.03) * mm, "end": v(-133.55, -116.03) * mm});
            skLineSegment(sketch, "E51.21.13.0", {"start": v(-135.13, -217.63) * mm, "end": v(-133.55, -217.63) * mm});
            skLineSegment(sketch, "E51.24.13.0", {"start": v(-135.13, -173.18) * mm, "end": v(-133.55, -173.18) * mm});
            skLineSegment(sketch, "E51.27.13.0", {"start": v(-135.13, -160.48) * mm, "end": v(-133.55, -160.48) * mm});
            skLineSegment(sketch, "E51.30.13.0", {"start": v(-131.96, -208.1) * mm, "end": v(-130.37, -208.1) * mm});
            skLineSegment(sketch, "E51.33.13.0", {"start": v(-131.96, -125.55) * mm, "end": v(-130.37, -125.55) * mm});
            skLineSegment(sketch, "E51.0.14.0", {"start": v(-139.9, -217.63) * mm, "end": v(-139.9, -173.18) * mm});
            skLineSegment(sketch, "E51.3.14.0", {"start": v(-139.9, -116.03) * mm, "end": v(-139.9, -160.48) * mm});
            skLineSegment(sketch, "E51.6.14.0", {"start": v(-136.72, -125.55) * mm, "end": v(-136.72, -208.1) * mm});
            skLineSegment(sketch, "E51.9.14.0", {"start": v(-141.48, -116.03) * mm, "end": v(-141.48, -160.48) * mm});
            skLineSegment(sketch, "E51.12.14.0", {"start": v(-138.3, -125.55) * mm, "end": v(-138.3, -208.1) * mm});
            skLineSegment(sketch, "E51.15.14.0", {"start": v(-141.48, -217.63) * mm, "end": v(-141.48, -173.18) * mm});
            skLineSegment(sketch, "E51.18.14.0", {"start": v(-141.48, -116.03) * mm, "end": v(-139.9, -116.03) * mm});
            skLineSegment(sketch, "E51.21.14.0", {"start": v(-141.48, -217.63) * mm, "end": v(-139.9, -217.63) * mm});
            skLineSegment(sketch, "E51.24.14.0", {"start": v(-141.48, -173.18) * mm, "end": v(-139.9, -173.18) * mm});
            skLineSegment(sketch, "E51.27.14.0", {"start": v(-141.48, -160.48) * mm, "end": v(-139.9, -160.48) * mm});
            skLineSegment(sketch, "E51.30.14.0", {"start": v(-138.3, -208.1) * mm, "end": v(-136.72, -208.1) * mm});
            skLineSegment(sketch, "E51.33.14.0", {"start": v(-138.3, -125.55) * mm, "end": v(-136.72, -125.55) * mm});
            skLineSegment(sketch, "E51.0.15.0", {"start": v(-146.25, -217.63) * mm, "end": v(-146.25, -173.18) * mm});
            skLineSegment(sketch, "E51.3.15.0", {"start": v(-146.25, -116.03) * mm, "end": v(-146.25, -160.48) * mm});
            skLineSegment(sketch, "E51.6.15.0", {"start": v(-143.07, -125.55) * mm, "end": v(-143.07, -208.1) * mm});
            skLineSegment(sketch, "E51.9.15.0", {"start": v(-147.83, -116.03) * mm, "end": v(-147.83, -160.48) * mm});
            skLineSegment(sketch, "E51.12.15.0", {"start": v(-144.66, -125.55) * mm, "end": v(-144.66, -208.1) * mm});
            skLineSegment(sketch, "E51.15.15.0", {"start": v(-147.83, -217.63) * mm, "end": v(-147.83, -173.18) * mm});
            skLineSegment(sketch, "E51.18.15.0", {"start": v(-147.83, -116.03) * mm, "end": v(-146.25, -116.03) * mm});
            skLineSegment(sketch, "E51.21.15.0", {"start": v(-147.83, -217.63) * mm, "end": v(-146.25, -217.63) * mm});
            skLineSegment(sketch, "E51.24.15.0", {"start": v(-147.83, -173.18) * mm, "end": v(-146.25, -173.18) * mm});
            skLineSegment(sketch, "E51.27.15.0", {"start": v(-147.83, -160.48) * mm, "end": v(-146.25, -160.48) * mm});
            skLineSegment(sketch, "E51.30.15.0", {"start": v(-144.66, -208.1) * mm, "end": v(-143.07, -208.1) * mm});
            skLineSegment(sketch, "E51.33.15.0", {"start": v(-144.66, -125.55) * mm, "end": v(-143.07, -125.55) * mm});
            skLineSegment(sketch, "E51.0.16.0", {"start": v(-152.6, -217.63) * mm, "end": v(-152.6, -173.18) * mm});
            skLineSegment(sketch, "E51.3.16.0", {"start": v(-152.6, -116.03) * mm, "end": v(-152.6, -160.48) * mm});
            skLineSegment(sketch, "E51.6.16.0", {"start": v(-149.42, -125.55) * mm, "end": v(-149.42, -208.1) * mm});
            skLineSegment(sketch, "E51.9.16.0", {"start": v(-154.18, -116.03) * mm, "end": v(-154.18, -160.48) * mm});
            skLineSegment(sketch, "E51.12.16.0", {"start": v(-151, -125.55) * mm, "end": v(-151, -208.1) * mm});
            skLineSegment(sketch, "E51.15.16.0", {"start": v(-154.18, -217.63) * mm, "end": v(-154.18, -173.18) * mm});
            skLineSegment(sketch, "E51.18.16.0", {"start": v(-154.18, -116.03) * mm, "end": v(-152.6, -116.03) * mm});
            skLineSegment(sketch, "E51.21.16.0", {"start": v(-154.18, -217.63) * mm, "end": v(-152.6, -217.63) * mm});
            skLineSegment(sketch, "E51.24.16.0", {"start": v(-154.18, -173.18) * mm, "end": v(-152.6, -173.18) * mm});
            skLineSegment(sketch, "E51.27.16.0", {"start": v(-154.18, -160.48) * mm, "end": v(-152.6, -160.48) * mm});
            skLineSegment(sketch, "E51.30.16.0", {"start": v(-151, -208.1) * mm, "end": v(-149.42, -208.1) * mm});
            skLineSegment(sketch, "E51.33.16.0", {"start": v(-151, -125.55) * mm, "end": v(-149.42, -125.55) * mm});
            skLineSegment(sketch, "E51.0.17.0", {"start": v(-158.95, -217.63) * mm, "end": v(-158.95, -173.18) * mm});
            skLineSegment(sketch, "E51.3.17.0", {"start": v(-158.95, -116.03) * mm, "end": v(-158.95, -160.48) * mm});
            skLineSegment(sketch, "E51.6.17.0", {"start": v(-155.77, -125.55) * mm, "end": v(-155.77, -208.1) * mm});
            skLineSegment(sketch, "E51.9.17.0", {"start": v(-160.53, -116.03) * mm, "end": v(-160.53, -160.48) * mm});
            skLineSegment(sketch, "E51.12.17.0", {"start": v(-157.36, -125.55) * mm, "end": v(-157.36, -208.1) * mm});
            skLineSegment(sketch, "E51.15.17.0", {"start": v(-160.53, -217.63) * mm, "end": v(-160.53, -173.18) * mm});
            skLineSegment(sketch, "E51.18.17.0", {"start": v(-160.53, -116.03) * mm, "end": v(-158.95, -116.03) * mm});
            skLineSegment(sketch, "E51.21.17.0", {"start": v(-160.53, -217.63) * mm, "end": v(-158.95, -217.63) * mm});
            skLineSegment(sketch, "E51.24.17.0", {"start": v(-160.53, -173.18) * mm, "end": v(-158.95, -173.18) * mm});
            skLineSegment(sketch, "E51.27.17.0", {"start": v(-160.53, -160.48) * mm, "end": v(-158.95, -160.48) * mm});
            skLineSegment(sketch, "E51.30.17.0", {"start": v(-157.36, -208.1) * mm, "end": v(-155.77, -208.1) * mm});
            skLineSegment(sketch, "E51.33.17.0", {"start": v(-157.36, -125.55) * mm, "end": v(-155.77, -125.55) * mm});
            skLineSegment(sketch, "E52.1.0.0", {"start": v(-103.38, -217.63) * mm, "end": v(-103.38, -173.18) * mm});
            skLineSegment(sketch, "E52.1.0.1", {"start": v(-103.38, -116.03) * mm, "end": v(-103.38, -160.48) * mm});
            skLineSegment(sketch, "E52.1.0.2", {"start": v(-101.8, -116.03) * mm, "end": v(-101.8, -160.48) * mm});
            skLineSegment(sketch, "E52.1.0.3", {"start": v(-101.8, -217.63) * mm, "end": v(-101.8, -173.18) * mm});
            skLineSegment(sketch, "E52.1.0.4", {"start": v(-103.38, -217.63) * mm, "end": v(-101.8, -217.63) * mm});
            skLineSegment(sketch, "E52.1.0.5", {"start": v(-103.38, -173.18) * mm, "end": v(-101.8, -173.18) * mm});
            skLineSegment(sketch, "E52.1.0.6", {"start": v(-103.38, -160.48) * mm, "end": v(-101.8, -160.48) * mm});
            skLineSegment(sketch, "E52.1.0.7", {"start": v(-103.38, -116.03) * mm, "end": v(-101.8, -116.03) * mm});
            skLineSegment(sketch, "E52.direction1", {"start": v(-97.03, -217.63) * mm, "end": v(-103.38, -217.63) * mm, "construction": true});
            skLineSegment(sketch, "E53.1.0.0", {"start": v(-163.7, -125.55) * mm, "end": v(-162.12, -125.55) * mm});
            skLineSegment(sketch, "E53.1.0.1", {"start": v(-163.7, -208.1) * mm, "end": v(-162.12, -208.1) * mm});
            skLineSegment(sketch, "E53.1.0.2", {"start": v(-163.7, -125.55) * mm, "end": v(-163.7, -208.1) * mm});
            skLineSegment(sketch, "E53.1.0.3", {"start": v(-162.12, -125.55) * mm, "end": v(-162.12, -208.1) * mm});
            skLineSegment(sketch, "E53.direction1", {"start": v(-157.36, -208.1) * mm, "end": v(-163.7, -208.1) * mm, "construction": true});
            skSolve(sketch);
        }
        {
            var Q0;
            {var subQ124=sQuery(id+"F0.wireOp",EDGE,"E1.top");Q0=makeQuery(id+"F0.imprint","IMPRINT",FACE,{"disambiguationData":[TD([[makeQuery(id+"F0.imprint","IMPRINT",EDGE,{"derivedFrom":subQ124}),-1.0]])]});}
            var Q1;
            Q1=makeQuery(id+"F0.imprint","IMPRINT",FACE,{"disambiguationData":[TD([[makeQuery(id+"F0.imprint","IMPRINT",EDGE,{"derivedFrom":sQuery(id+"F0.wireOp",EDGE,"E36.MirrorCS")}),-1.0]])]});
            var Q2;
            Q2=makeQuery(id+"F0.imprint","IMPRINT",FACE,{"disambiguationData":[TD([[makeQuery(id+"F0.imprint","IMPRINT",EDGE,{"derivedFrom":sQuery(id+"F0.wireOp",EDGE,"E39.MirrorCS")}),-1.0]])]});
            var Q3;
            Q3=makeQuery(id+"F0.imprint","IMPRINT",FACE,{"disambiguationData":[TD([[makeQuery(id+"F0.imprint","IMPRINT",EDGE,{"derivedFrom":sQuery(id+"F0.wireOp",EDGE,"E31.bottom")}),1.0]])]});
            var Q4;
            Q4=makeQuery(id+"F0.imprint","IMPRINT",FACE,{"disambiguationData":[TD([[makeQuery(id+"F0.imprint","IMPRINT",EDGE,{"derivedFrom":sQuery(id+"F0.wireOp",EDGE,"E33.bottom")}),1.0]])]});
            var Q5;
            Q5=makeQuery(id+"F0.imprint","IMPRINT",FACE,{"disambiguationData":[TD([[makeQuery(id+"F0.imprint","IMPRINT",EDGE,{"derivedFrom":sQuery(id+"F0.wireOp",EDGE,"E30.bottom")}),-1.0]])]});
            var Q6;
            Q6=makeQuery(id+"F0.imprint","IMPRINT",FACE,{"disambiguationData":[TD([[makeQuery(id+"F0.imprint","IMPRINT",EDGE,{"derivedFrom":sQuery(id+"F0.wireOp",EDGE,"E29.bottom")}),-1.0]])]});
            var Q7;
            {var subQ5=sQuery(id+"F0.wireOp",EDGE,"E27.MirrorCS");Q7=makeQuery(id+"F0.imprint","IMPRINT",FACE,{"disambiguationData":[TD([[makeQuery(id+"F0.imprint","IMPRINT",EDGE,{"derivedFrom":subQ5}),1.0]])]});}
            var Q8;
            Q8=makeQuery(id+"F0.imprint","IMPRINT",FACE,{"disambiguationData":[TD([[makeQuery(id+"F0.imprint","IMPRINT",EDGE,{"derivedFrom":sQuery(id+"F0.wireOp",EDGE,"E10.0.2.6")}),1.0]])]});
            var Q9;
            Q9=makeQuery(id+"F0.imprint","IMPRINT",FACE,{"disambiguationData":[TD([[makeQuery(id+"F0.imprint","IMPRINT",EDGE,{"derivedFrom":sQuery(id+"F0.wireOp",EDGE,"E10.0.2.2")}),-1.0]])]});
            var Q10;
            Q10=makeQuery(id+"F0.imprint","IMPRINT",FACE,{"disambiguationData":[TD([[makeQuery(id+"F0.imprint","IMPRINT",EDGE,{"derivedFrom":sQuery(id+"F0.wireOp",EDGE,"E10.0.1.2")}),-1.0]])]});
            var Q11;
            Q11=makeQuery(id+"F0.imprint","IMPRINT",FACE,{"disambiguationData":[TD([[makeQuery(id+"F0.imprint","IMPRINT",EDGE,{"derivedFrom":sQuery(id+"F0.wireOp",EDGE,"E10.0.1.6")}),1.0]])]});
            var Q12;
            Q12=makeQuery(id+"F0.imprint","IMPRINT",FACE,{"disambiguationData":[TD([[makeQuery(id+"F0.imprint","IMPRINT",EDGE,{"derivedFrom":sQuery(id+"F0.wireOp",EDGE,"E8.top")}),1.0]])]});
            var Q13;
            Q13=makeQuery(id+"F0.imprint","IMPRINT",FACE,{"disambiguationData":[TD([[makeQuery(id+"F0.imprint","IMPRINT",EDGE,{"derivedFrom":sQuery(id+"F0.wireOp",EDGE,"E7.bottom")}),1.0]])]});
            var Q14;
            {var subQ5=sQuery(id+"F0.wireOp",EDGE,"E15.left");Q14=makeQuery(id+"F0.imprint","IMPRINT",FACE,{"disambiguationData":[TD([[makeQuery(id+"F0.imprint","IMPRINT",EDGE,{"derivedFrom":subQ5}),-1.0]])]});}
            extrude(context, id + "F1", {"entities" : qUnion([Q0, Q1, Q2, Q3, Q4, Q5, Q6, Q7, Q8, Q9, Q10, Q11, Q12, Q13, Q14]), "depth" : 3.17 * mm});
        }
    });
